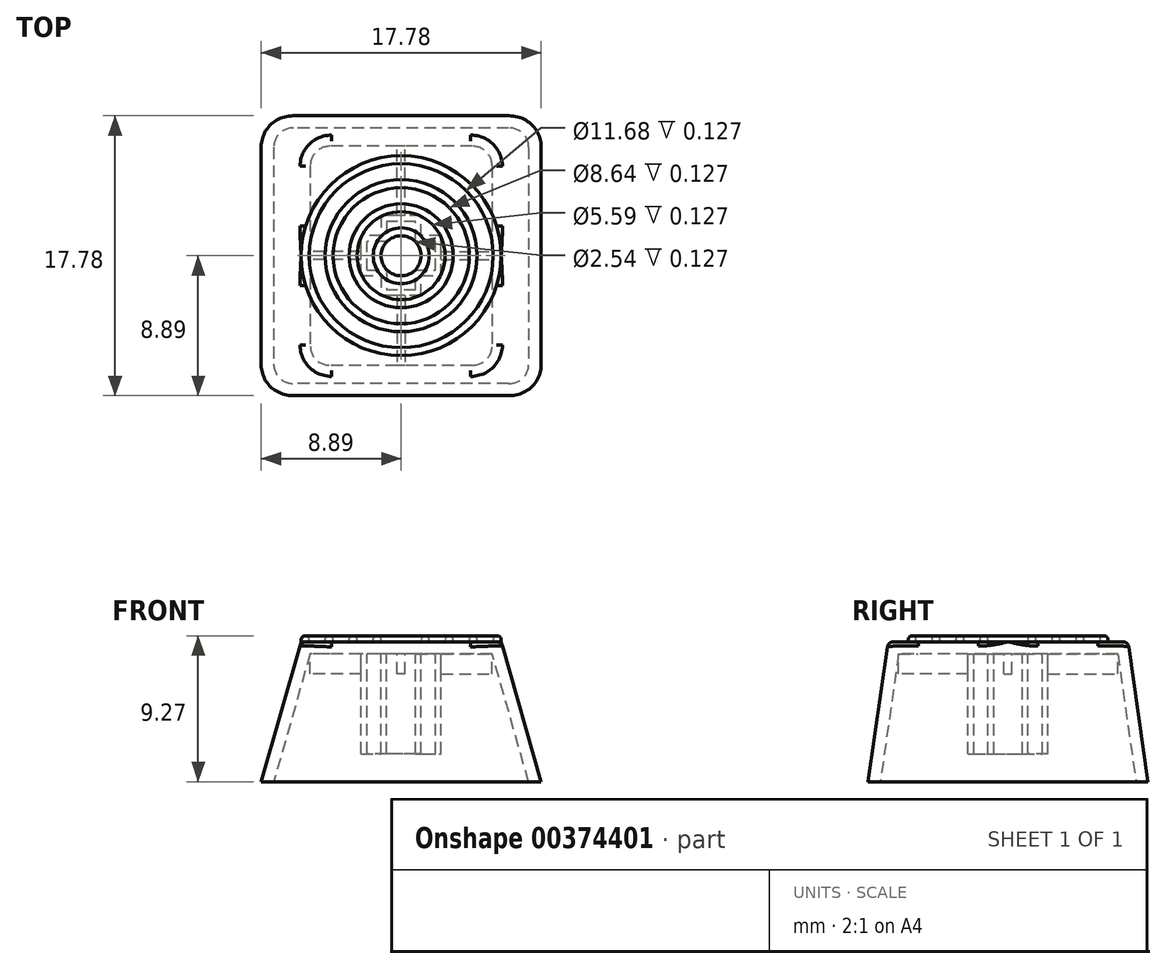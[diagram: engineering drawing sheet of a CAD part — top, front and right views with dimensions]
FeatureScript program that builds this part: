
annotation { "Feature Type Name" : "Feature", "Feature Type Description" : "" }
export const myFeature = defineFeature(function(context is Context, id is Id, definition is map)
    precondition{}
    {
        {
            var Q0;
            Q0=qCreatedBy(makeId("Top.planeOp"),FACE);
            var sketch = newSketch(context, id + "F0", { "sketchPlane" : qUnion([Q0])});
            skLineSegment(sketch, "E0.bottom", {"start": v(8.9, 8.9) * mm, "end": v(-8.9, 8.9) * mm});
            skLineSegment(sketch, "E0.top", {"start": v(8.9, -8.89) * mm, "end": v(-8.9, -8.89) * mm});
            skLineSegment(sketch, "E0.left", {"start": v(8.9, 8.89) * mm, "end": v(8.9, -8.89) * mm});
            skLineSegment(sketch, "E0.right", {"start": v(-8.9, 8.9) * mm, "end": v(-8.9, -8.89) * mm});
            skPoint(sketch, "E0.middle", {"position": v(0, 0) * mm});
            skSolve(sketch);
        }
        {
            var Q0;
            Q0=makeQuery(id+"F0.imprint","IMPRINT",FACE,{"disambiguationData":[TD([[makeQuery(id+"F0.imprint","IMPRINT",EDGE,{"derivedFrom":sQuery(id+"F0.wireOp",EDGE,"E0.bottom")}),1.0]])]});
            cPlane(context, id + "F1", {"entities" : qUnion([Q0]), "cplaneType" : CPlaneType.OFFSET, "offset" : 8.9 * mm, "width" : 152.4 * mm, "height" : 152.4 * mm});
        }
        {
            var Q0;
            Q0=qCreatedBy(id+"F1.planeOp",FACE);
            var sketch = newSketch(context, id + "F2", { "sketchPlane" : qUnion([Q0])});
            skLineSegment(sketch, "E1.bottom", {"start": v(6.35, 7.62) * mm, "end": v(-6.35, 7.62) * mm});
            skLineSegment(sketch, "E1.top", {"start": v(6.35, -7.62) * mm, "end": v(-6.35, -7.62) * mm});
            skLineSegment(sketch, "E1.left", {"start": v(6.35, 7.62) * mm, "end": v(6.35, -7.62) * mm});
            skLineSegment(sketch, "E1.right", {"start": v(-6.35, 7.62) * mm, "end": v(-6.35, -7.62) * mm});
            skPoint(sketch, "E1.middle", {"position": v(0, 0) * mm});
            skSolve(sketch);
        }
        {
            var Q0;
            Q0=makeQuery(id+"F2.imprint","IMPRINT",FACE,{"disambiguationData":[TD([[makeQuery(id+"F2.imprint","IMPRINT",EDGE,{"derivedFrom":sQuery(id+"F2.wireOp",EDGE,"E1.bottom")}),1.0]])]});
            var Q1;
            Q1=makeQuery(id+"F0.imprint","IMPRINT",FACE,{"disambiguationData":[TD([[makeQuery(id+"F0.imprint","IMPRINT",EDGE,{"derivedFrom":sQuery(id+"F0.wireOp",EDGE,"E0.bottom")}),1.0]])]});
            loft(context, id + "F3", {"sheetProfilesArray" : [{ "sheetProfileEntities" : qUnion([Q0]) }, { "sheetProfileEntities" : qUnion([Q1]) }]});
        }
        {
            var Q0;
            Q0=makeQuery(id+"F3.opLoft","SWEPT_EDGE",EDGE,{"disambiguationData":[OSD([sQuery(id+"F0.wireOp",EDGE,"E0.bottom"),sQuery(id+"F0.wireOp",EDGE,"E0.right"),sQuery(id+"F2.wireOp",EDGE,"E1.bottom"),sQuery(id+"F2.wireOp",EDGE,"E1.right")])]});
            var Q1;
            Q1=makeQuery(id+"F3.opLoft","SWEPT_EDGE",EDGE,{"disambiguationData":[OSD([sQuery(id+"F0.wireOp",EDGE,"E0.bottom"),sQuery(id+"F0.wireOp",EDGE,"E0.left"),sQuery(id+"F2.wireOp",EDGE,"E1.bottom"),sQuery(id+"F2.wireOp",EDGE,"E1.left")])]});
            var Q2;
            Q2=makeQuery(id+"F3.opLoft","SWEPT_EDGE",EDGE,{"disambiguationData":[OSD([sQuery(id+"F0.wireOp",EDGE,"E0.top"),sQuery(id+"F0.wireOp",EDGE,"E0.left"),sQuery(id+"F2.wireOp",EDGE,"E1.top"),sQuery(id+"F2.wireOp",EDGE,"E1.left")])]});
            var Q3;
            Q3=makeQuery(id+"F3.opLoft","SWEPT_EDGE",EDGE,{"disambiguationData":[OSD([sQuery(id+"F0.wireOp",EDGE,"E0.top"),sQuery(id+"F0.wireOp",EDGE,"E0.right"),sQuery(id+"F2.wireOp",EDGE,"E1.top"),sQuery(id+"F2.wireOp",EDGE,"E1.right")])]});
            fillet(context, id + "F4", {"entities" : qUnion([Q0, Q1, Q2, Q3]), "radius" : 2.03 * mm, "tangentPropagation" : true, "allowEdgeOverflow" : false});
        }
        {
            var Q0;
            Q0=makeQuery(id+"F3.opLoft","CAP_FACE",FACE,{"disambiguationData":[OSD([makeQuery(id+"F0.imprint","IMPRINT",FACE,{"disambiguationData":[TD([[makeQuery(id+"F0.imprint","IMPRINT",EDGE,{"derivedFrom":sQuery(id+"F0.wireOp",EDGE,"E0.bottom")}),1.0]])]})])],"isStart":true});
            shell(context, id + "F5", {"entities" : qUnion([Q0]), "thickness" : 0.76 * mm});
        }
        {
            var Q0;
            Q0=makeQuery(id+"F5.opShell","OFFSET_FACE",FACE,{"disambiguationData":[OSD([makeQuery(id+"F2.imprint","IMPRINT",FACE,{"disambiguationData":[TD([[makeQuery(id+"F2.imprint","IMPRINT",EDGE,{"derivedFrom":sQuery(id+"F2.wireOp",EDGE,"E1.bottom")}),1.0]])]})])]});
            var sketch = newSketch(context, id + "F6", { "sketchPlane" : qUnion([Q0])});
            skLineSegment(sketch, "E2.left", {"start": v(2.54, 1.27) * mm, "end": v(2.54, -1.27) * mm});
            skLineSegment(sketch, "E2.right", {"start": v(-2.54, 1.27) * mm, "end": v(-2.54, -1.27) * mm});
            skPoint(sketch, "E2.middle", {"position": v(0, 0) * mm});
            skLineSegment(sketch, "E3.bottom", {"start": v(1.27, 2.54) * mm, "end": v(-1.27, 2.54) * mm});
            skLineSegment(sketch, "E3.top", {"start": v(1.27, -2.54) * mm, "end": v(-1.27, -2.54) * mm});
            skLineSegment(sketch, "E4", {"start": v(1.27, 2.54) * mm, "end": v(1.27, 1.27) * mm});
            skLineSegment(sketch, "E5", {"start": v(1.27, -1.27) * mm, "end": v(1.27, -2.54) * mm});
            skLineSegment(sketch, "E6", {"start": v(-1.27, -2.54) * mm, "end": v(-1.27, -1.27) * mm});
            skLineSegment(sketch, "E7", {"start": v(-1.27, 1.27) * mm, "end": v(-1.27, 2.54) * mm});
            skLineSegment(sketch, "E8", {"start": v(-2.54, 1.27) * mm, "end": v(-1.27, 1.27) * mm});
            skLineSegment(sketch, "E9", {"start": v(1.27, 1.27) * mm, "end": v(2.54, 1.27) * mm});
            skLineSegment(sketch, "E10", {"start": v(2.54, -1.27) * mm, "end": v(1.27, -1.27) * mm});
            skLineSegment(sketch, "E11", {"start": v(-1.27, -1.27) * mm, "end": v(-2.54, -1.27) * mm});
            skLineSegment(sketch, "E12.0", {"start": v(-2.18, 0.91) * mm, "end": v(-0.91, 0.91) * mm});
            skLineSegment(sketch, "E12.1", {"start": v(2.18, 0.91) * mm, "end": v(2.18, -0.91) * mm});
            skLineSegment(sketch, "E12.2", {"start": v(0.91, 0.91) * mm, "end": v(2.18, 0.91) * mm});
            skLineSegment(sketch, "E12.3", {"start": v(0.91, 2.18) * mm, "end": v(0.91, 0.91) * mm});
            skLineSegment(sketch, "E12.4", {"start": v(0.91, 2.18) * mm, "end": v(-0.91, 2.18) * mm});
            skLineSegment(sketch, "E12.5", {"start": v(2.18, -0.91) * mm, "end": v(0.91, -0.91) * mm});
            skLineSegment(sketch, "E12.6", {"start": v(-0.91, 0.91) * mm, "end": v(-0.91, 2.18) * mm});
            skLineSegment(sketch, "E12.7", {"start": v(0.91, -0.91) * mm, "end": v(0.91, -2.18) * mm});
            skLineSegment(sketch, "E12.8", {"start": v(0.91, -2.18) * mm, "end": v(-0.91, -2.18) * mm});
            skLineSegment(sketch, "E12.9", {"start": v(-0.91, -2.18) * mm, "end": v(-0.91, -0.91) * mm});
            skLineSegment(sketch, "E12.10", {"start": v(-0.91, -0.91) * mm, "end": v(-2.18, -0.91) * mm});
            skLineSegment(sketch, "E12.11", {"start": v(-2.18, 0.91) * mm, "end": v(-2.18, -0.91) * mm});
            skSolve(sketch);
        }
        {
            var Q0;
            Q0=makeQuery(id+"F6.imprint","IMPRINT",FACE,{"disambiguationData":[TD([[makeQuery(id+"F6.imprint","IMPRINT",EDGE,{"derivedFrom":sQuery(id+"F6.wireOp",EDGE,"E2.left")}),-1.0]])]});
            extrude(context, id + "F7", {"entities" : qUnion([Q0]), "operationType" : NewBodyOperationType.ADD, "depth" : 6.35 * mm});
        }
        {
            var Q0;
            {var subQ6=sQuery(id+"F2.wireOp",EDGE,"E1.bottom");Q0=makeQuery(id+"F7.boolean.opBoolean","SPLIT",FACE,{"disambiguationData":[TD([makeQuery(id+"F7.opExtrude","SWEPT_FACE",FACE,{"disambiguationData":[OSD([sQuery(id+"F6.wireOp",EDGE,"E2.left")])]})])],"derivedFrom":makeQuery(id+"F5.opShell","OFFSET_FACE",FACE,{"disambiguationData":[OSD([makeQuery(id+"F2.imprint","IMPRINT",FACE,{"disambiguationData":[TD([[makeQuery(id+"F2.imprint","IMPRINT",EDGE,{"derivedFrom":subQ6}),1.0]])]})])]})});}
            var sketch = newSketch(context, id + "F8", { "sketchPlane" : qUnion([Q0])});
            skPoint(sketch, "E13", {"position": v(-4.16, 0) * mm});
            skPoint(sketch, "E14", {"position": v(4.16, 0) * mm});
            skPoint(sketch, "E15", {"position": v(0, 4.75) * mm});
            skLineSegment(sketch, "E16.bottom", {"start": v(-2.54, 0.25) * mm, "end": v(-5.78, 0.25) * mm});
            skLineSegment(sketch, "E16.top", {"start": v(-2.54, -0.25) * mm, "end": v(-5.78, -0.25) * mm});
            skLineSegment(sketch, "E16.left", {"start": v(-2.54, 0.25) * mm, "end": v(-2.54, -0.25) * mm});
            skLineSegment(sketch, "E16.right", {"start": v(-5.78, 0.25) * mm, "end": v(-5.78, -0.25) * mm});
            skLineSegment(sketch, "E17.bottom", {"start": v(0.25, 2.54) * mm, "end": v(-0.25, 2.54) * mm});
            skLineSegment(sketch, "E17.top", {"start": v(0.25, 6.96) * mm, "end": v(-0.25, 6.96) * mm});
            skLineSegment(sketch, "E17.left", {"start": v(0.25, 2.54) * mm, "end": v(0.25, 6.96) * mm});
            skLineSegment(sketch, "E17.right", {"start": v(-0.25, 2.54) * mm, "end": v(-0.25, 6.96) * mm});
            skLineSegment(sketch, "E18.bottom", {"start": v(2.54, 0.25) * mm, "end": v(5.78, 0.25) * mm});
            skLineSegment(sketch, "E18.top", {"start": v(2.54, -0.25) * mm, "end": v(5.78, -0.25) * mm});
            skLineSegment(sketch, "E18.left", {"start": v(2.54, 0.25) * mm, "end": v(2.54, -0.25) * mm});
            skLineSegment(sketch, "E18.right", {"start": v(5.78, 0.25) * mm, "end": v(5.78, -0.25) * mm});
            skLineSegment(sketch, "E19.bottom", {"start": v(-0.25, -2.54) * mm, "end": v(0.25, -2.54) * mm});
            skLineSegment(sketch, "E19.top", {"start": v(-0.25, -6.96) * mm, "end": v(0.25, -6.96) * mm});
            skLineSegment(sketch, "E19.left", {"start": v(-0.25, -2.54) * mm, "end": v(-0.25, -6.96) * mm});
            skLineSegment(sketch, "E19.right", {"start": v(0.25, -2.54) * mm, "end": v(0.25, -6.96) * mm});
            skPoint(sketch, "E19.middle", {"position": v(0, -4.75) * mm});
            skSolve(sketch);
        }
        {
            var Q0;
            Q0=makeQuery(id+"F8.imprint","IMPRINT",FACE,{"disambiguationData":[TD([[makeQuery(id+"F8.imprint","IMPRINT",EDGE,{"derivedFrom":sQuery(id+"F8.wireOp",EDGE,"E17.bottom")}),-1.0]])]});
            var Q1;
            Q1=makeQuery(id+"F8.imprint","IMPRINT",FACE,{"disambiguationData":[TD([[makeQuery(id+"F8.imprint","IMPRINT",EDGE,{"derivedFrom":sQuery(id+"F8.wireOp",EDGE,"E18.bottom")}),-1.0]])]});
            var Q2;
            Q2=makeQuery(id+"F8.imprint","IMPRINT",FACE,{"disambiguationData":[TD([[makeQuery(id+"F8.imprint","IMPRINT",EDGE,{"derivedFrom":sQuery(id+"F8.wireOp",EDGE,"E19.bottom")}),1.0]])]});
            var Q3;
            Q3=makeQuery(id+"F8.imprint","IMPRINT",FACE,{"disambiguationData":[TD([[makeQuery(id+"F8.imprint","IMPRINT",EDGE,{"derivedFrom":sQuery(id+"F8.wireOp",EDGE,"E16.bottom")}),1.0]])]});
            extrude(context, id + "F9", {"entities" : qUnion([Q0, Q1, Q2, Q3]), "operationType" : NewBodyOperationType.ADD, "depth" : 1.27 * mm});
        }
        {
            var Q0;
            Q0=makeQuery(id+"F3.opLoft","CAP_FACE",FACE,{"disambiguationData":[OSD([makeQuery(id+"F2.imprint","IMPRINT",FACE,{"disambiguationData":[TD([[makeQuery(id+"F2.imprint","IMPRINT",EDGE,{"derivedFrom":sQuery(id+"F2.wireOp",EDGE,"E1.bottom")}),1.0]])]})])],"isStart":true});
            var sketch = newSketch(context, id + "F10", { "sketchPlane" : qUnion([Q0])});
            skCircle(sketch, "E20", {"center": v(0, 0) * mm, "radius": 6.35 * mm});
            skCircle(sketch, "E21.0", {"center": v(0, 0) * mm, "radius": 5.84 * mm});
            skCircle(sketch, "E22.0", {"center": v(0, 0) * mm, "radius": 4.83 * mm});
            skCircle(sketch, "E23.0", {"center": v(0, 0) * mm, "radius": 4.32 * mm});
            skCircle(sketch, "E24.0", {"center": v(0, 0) * mm, "radius": 3.3 * mm});
            skCircle(sketch, "E25.0", {"center": v(0, 0) * mm, "radius": 2.8 * mm});
            skCircle(sketch, "E26.0", {"center": v(0, 0) * mm, "radius": 1.78 * mm});
            skCircle(sketch, "E27.0", {"center": v(0, 0) * mm, "radius": 1.27 * mm});
            skSolve(sketch);
        }
        {
            var Q0;
            Q0=makeQuery(id+"F10.imprint","IMPRINT",FACE,{"disambiguationData":[TD([[makeQuery(id+"F10.imprint","IMPRINT",EDGE,{"derivedFrom":sQuery(id+"F10.wireOp",EDGE,"E21.0")}),-1.0]])]});
            var Q1;
            Q1=makeQuery(id+"F10.imprint","IMPRINT",FACE,{"disambiguationData":[TD([[makeQuery(id+"F10.imprint","IMPRINT",EDGE,{"derivedFrom":sQuery(id+"F10.wireOp",EDGE,"E22.0")}),1.0]])]});
            var Q2;
            Q2=makeQuery(id+"F10.imprint","IMPRINT",FACE,{"disambiguationData":[TD([[makeQuery(id+"F10.imprint","IMPRINT",EDGE,{"derivedFrom":sQuery(id+"F10.wireOp",EDGE,"E24.0")}),1.0]])]});
            var Q3;
            Q3=makeQuery(id+"F10.imprint","IMPRINT",FACE,{"disambiguationData":[TD([[makeQuery(id+"F10.imprint","IMPRINT",EDGE,{"derivedFrom":sQuery(id+"F10.wireOp",EDGE,"E26.0")}),1.0]])]});
            extrude(context, id + "F11", {"entities" : qUnion([Q0, Q1, Q2, Q3]), "operationType" : NewBodyOperationType.ADD, "depth" : 0.38 * mm});
        }
        {
            var Q0;
            Q0=makeQuery(id+"F11.opExtrude","CAP_EDGE",EDGE,{"disambiguationData":[OSD([sQuery(id+"F10.wireOp",EDGE,"E21.0")])],"isStart":false});
            var Q1;
            Q1=makeQuery(id+"F11.opExtrude","CAP_EDGE",EDGE,{"disambiguationData":[OSD([sQuery(id+"F10.wireOp",EDGE,"E20")])],"isStart":false});
            var Q2;
            Q2=makeQuery(id+"F11.opExtrude","CAP_EDGE",EDGE,{"disambiguationData":[OSD([sQuery(id+"F10.wireOp",EDGE,"E22.0")])],"isStart":false});
            var Q3;
            Q3=makeQuery(id+"F11.opExtrude","CAP_EDGE",EDGE,{"disambiguationData":[OSD([sQuery(id+"F10.wireOp",EDGE,"E23.0")])],"isStart":false});
            var Q4;
            Q4=makeQuery(id+"F11.opExtrude","CAP_EDGE",EDGE,{"disambiguationData":[OSD([sQuery(id+"F10.wireOp",EDGE,"E24.0")])],"isStart":false});
            var Q5;
            Q5=makeQuery(id+"F11.opExtrude","CAP_EDGE",EDGE,{"disambiguationData":[OSD([sQuery(id+"F10.wireOp",EDGE,"E25.0")])],"isStart":false});
            var Q6;
            Q6=makeQuery(id+"F11.opExtrude","CAP_EDGE",EDGE,{"disambiguationData":[OSD([sQuery(id+"F10.wireOp",EDGE,"E26.0")])],"isStart":false});
            var Q7;
            Q7=makeQuery(id+"F11.opExtrude","CAP_EDGE",EDGE,{"disambiguationData":[OSD([sQuery(id+"F10.wireOp",EDGE,"E27.0")])],"isStart":false});
            fillet(context, id + "F12", {"entities" : qUnion([Q0, Q1, Q2, Q3, Q4, Q5, Q6, Q7]), "radius" : 0.25 * mm, "tangentPropagation" : true, "allowEdgeOverflow" : false});
        }
        {
            var Q0;
            {var subQ0=sQuery(id+"F2.wireOp",EDGE,"E1.left");var subQ1=sQuery(id+"F2.wireOp",EDGE,"E1.top");var subQ2=sQuery(id+"F2.wireOp",EDGE,"E1.bottom");var subQ3=sQuery(id+"F0.wireOp",EDGE,"E0.left");var subQ4=sQuery(id+"F0.wireOp",EDGE,"E0.top");Q0=makeQuery(id+"F11.boolean.opBoolean","SPLIT",EDGE,{"disambiguationData":[TD([makeQuery(id+"F4.opFillet","BLEND_FACE",FACE,{"disambiguationData":[OSD([subQ4,subQ3,subQ1,subQ0])]})])],"derivedFrom":makeQuery(id+"F3.opLoft","MID_CAP_EDGE",EDGE,{"disambiguationData":[OSD([subQ2,subQ1,subQ0])],"capPos":0.0})});}
            var Q1;
            {var subQ0=sQuery(id+"F2.wireOp",EDGE,"E1.top");var subQ1=sQuery(id+"F2.wireOp",EDGE,"E1.left");Q1=makeQuery(id+"F4.opFillet","BLEND_EDGE",EDGE,{"blendedFrom":[makeQuery(id+"F3.opLoft","SWEPT_EDGE",EDGE,{"disambiguationData":[OSD([sQuery(id+"F0.wireOp",EDGE,"E0.top"),sQuery(id+"F0.wireOp",EDGE,"E0.left"),subQ0,subQ1])]}),makeQuery(id+"F3.opLoft","CAP_FACE",FACE,{"disambiguationData":[OSD([makeQuery(id+"F2.imprint","IMPRINT",FACE,{"disambiguationData":[TD([[makeQuery(id+"F2.imprint","IMPRINT",EDGE,{"derivedFrom":sQuery(id+"F2.wireOp",EDGE,"E1.bottom")}),1.0]])]})])],"isStart":true})],"blendedInto":[makeQuery(id+"F3.opLoft","CAP_FACE",FACE,{"disambiguationData":[OSD([makeQuery(id+"F2.imprint","IMPRINT",FACE,{"disambiguationData":[TD([[makeQuery(id+"F2.imprint","IMPRINT",EDGE,{"derivedFrom":sQuery(id+"F2.wireOp",EDGE,"E1.bottom")}),1.0]])]})])],"isStart":true})]});}
            var Q2;
            Q2=makeQuery(id+"F3.opLoft","MID_CAP_EDGE",EDGE,{"disambiguationData":[OSD([sQuery(id+"F2.wireOp",EDGE,"E1.top"),sQuery(id+"F2.wireOp",EDGE,"E1.left"),sQuery(id+"F2.wireOp",EDGE,"E1.right")])],"capPos":0.0});
            var Q3;
            {var subQ0=sQuery(id+"F2.wireOp",EDGE,"E1.left");var subQ1=sQuery(id+"F2.wireOp",EDGE,"E1.top");var subQ2=sQuery(id+"F2.wireOp",EDGE,"E1.bottom");var subQ3=sQuery(id+"F0.wireOp",EDGE,"E0.left");var subQ4=sQuery(id+"F0.wireOp",EDGE,"E0.bottom");Q3=makeQuery(id+"F11.boolean.opBoolean","SPLIT",EDGE,{"disambiguationData":[TD([makeQuery(id+"F4.opFillet","BLEND_FACE",FACE,{"disambiguationData":[OSD([subQ4,subQ3,subQ2,subQ0])]})])],"derivedFrom":makeQuery(id+"F3.opLoft","MID_CAP_EDGE",EDGE,{"disambiguationData":[OSD([subQ2,subQ1,subQ0])],"capPos":0.0})});}
            var Q4;
            {var subQ0=sQuery(id+"F2.wireOp",EDGE,"E1.bottom");var subQ1=sQuery(id+"F2.wireOp",EDGE,"E1.left");Q4=makeQuery(id+"F4.opFillet","BLEND_EDGE",EDGE,{"blendedFrom":[makeQuery(id+"F3.opLoft","SWEPT_EDGE",EDGE,{"disambiguationData":[OSD([sQuery(id+"F0.wireOp",EDGE,"E0.bottom"),sQuery(id+"F0.wireOp",EDGE,"E0.left"),subQ0,subQ1])]}),makeQuery(id+"F3.opLoft","CAP_FACE",FACE,{"disambiguationData":[OSD([makeQuery(id+"F2.imprint","IMPRINT",FACE,{"disambiguationData":[TD([[makeQuery(id+"F2.imprint","IMPRINT",EDGE,{"derivedFrom":subQ0}),1.0]])]})])],"isStart":true})],"blendedInto":[makeQuery(id+"F3.opLoft","CAP_FACE",FACE,{"disambiguationData":[OSD([makeQuery(id+"F2.imprint","IMPRINT",FACE,{"disambiguationData":[TD([[makeQuery(id+"F2.imprint","IMPRINT",EDGE,{"derivedFrom":subQ0}),1.0]])]})])],"isStart":true})]});}
            var Q5;
            Q5=makeQuery(id+"F3.opLoft","MID_CAP_EDGE",EDGE,{"disambiguationData":[OSD([sQuery(id+"F2.wireOp",EDGE,"E1.bottom"),sQuery(id+"F2.wireOp",EDGE,"E1.left"),sQuery(id+"F2.wireOp",EDGE,"E1.right")])],"capPos":0.0});
            var Q6;
            {var subQ0=sQuery(id+"F2.wireOp",EDGE,"E1.bottom");var subQ1=sQuery(id+"F2.wireOp",EDGE,"E1.right");Q6=makeQuery(id+"F4.opFillet","BLEND_EDGE",EDGE,{"blendedFrom":[makeQuery(id+"F3.opLoft","SWEPT_EDGE",EDGE,{"disambiguationData":[OSD([sQuery(id+"F0.wireOp",EDGE,"E0.bottom"),sQuery(id+"F0.wireOp",EDGE,"E0.right"),subQ0,subQ1])]}),makeQuery(id+"F3.opLoft","CAP_FACE",FACE,{"disambiguationData":[OSD([makeQuery(id+"F2.imprint","IMPRINT",FACE,{"disambiguationData":[TD([[makeQuery(id+"F2.imprint","IMPRINT",EDGE,{"derivedFrom":subQ0}),1.0]])]})])],"isStart":true})],"blendedInto":[makeQuery(id+"F3.opLoft","CAP_FACE",FACE,{"disambiguationData":[OSD([makeQuery(id+"F2.imprint","IMPRINT",FACE,{"disambiguationData":[TD([[makeQuery(id+"F2.imprint","IMPRINT",EDGE,{"derivedFrom":subQ0}),1.0]])]})])],"isStart":true})]});}
            var Q7;
            {var subQ0=sQuery(id+"F2.wireOp",EDGE,"E1.right");var subQ1=sQuery(id+"F2.wireOp",EDGE,"E1.top");var subQ2=sQuery(id+"F2.wireOp",EDGE,"E1.bottom");var subQ3=sQuery(id+"F0.wireOp",EDGE,"E0.right");var subQ4=sQuery(id+"F0.wireOp",EDGE,"E0.bottom");Q7=makeQuery(id+"F11.boolean.opBoolean","SPLIT",EDGE,{"disambiguationData":[TD([makeQuery(id+"F4.opFillet","BLEND_FACE",FACE,{"disambiguationData":[OSD([subQ4,subQ3,subQ2,subQ0])]})])],"derivedFrom":makeQuery(id+"F3.opLoft","MID_CAP_EDGE",EDGE,{"disambiguationData":[OSD([subQ2,subQ1,subQ0])],"capPos":0.0})});}
            var Q8;
            {var subQ0=sQuery(id+"F2.wireOp",EDGE,"E1.right");var subQ1=sQuery(id+"F2.wireOp",EDGE,"E1.top");var subQ2=sQuery(id+"F2.wireOp",EDGE,"E1.bottom");var subQ3=sQuery(id+"F0.wireOp",EDGE,"E0.right");var subQ4=sQuery(id+"F0.wireOp",EDGE,"E0.top");Q8=makeQuery(id+"F11.boolean.opBoolean","SPLIT",EDGE,{"disambiguationData":[TD([makeQuery(id+"F4.opFillet","BLEND_FACE",FACE,{"disambiguationData":[OSD([subQ4,subQ3,subQ1,subQ0])]})])],"derivedFrom":makeQuery(id+"F3.opLoft","MID_CAP_EDGE",EDGE,{"disambiguationData":[OSD([subQ2,subQ1,subQ0])],"capPos":0.0})});}
            var Q9;
            {var subQ0=sQuery(id+"F2.wireOp",EDGE,"E1.top");var subQ1=sQuery(id+"F2.wireOp",EDGE,"E1.right");Q9=makeQuery(id+"F4.opFillet","BLEND_EDGE",EDGE,{"blendedFrom":[makeQuery(id+"F3.opLoft","SWEPT_EDGE",EDGE,{"disambiguationData":[OSD([sQuery(id+"F0.wireOp",EDGE,"E0.top"),sQuery(id+"F0.wireOp",EDGE,"E0.right"),subQ0,subQ1])]}),makeQuery(id+"F3.opLoft","CAP_FACE",FACE,{"disambiguationData":[OSD([makeQuery(id+"F2.imprint","IMPRINT",FACE,{"disambiguationData":[TD([[makeQuery(id+"F2.imprint","IMPRINT",EDGE,{"derivedFrom":sQuery(id+"F2.wireOp",EDGE,"E1.bottom")}),1.0]])]})])],"isStart":true})],"blendedInto":[makeQuery(id+"F3.opLoft","CAP_FACE",FACE,{"disambiguationData":[OSD([makeQuery(id+"F2.imprint","IMPRINT",FACE,{"disambiguationData":[TD([[makeQuery(id+"F2.imprint","IMPRINT",EDGE,{"derivedFrom":sQuery(id+"F2.wireOp",EDGE,"E1.bottom")}),1.0]])]})])],"isStart":true})]});}
            fillet(context, id + "F13", {"entities" : qUnion([Q0, Q1, Q2, Q3, Q4, Q5, Q6, Q7, Q8, Q9]), "radius" : 0.38 * mm, "tangentPropagation" : true, "allowEdgeOverflow" : false});
        }
    });
